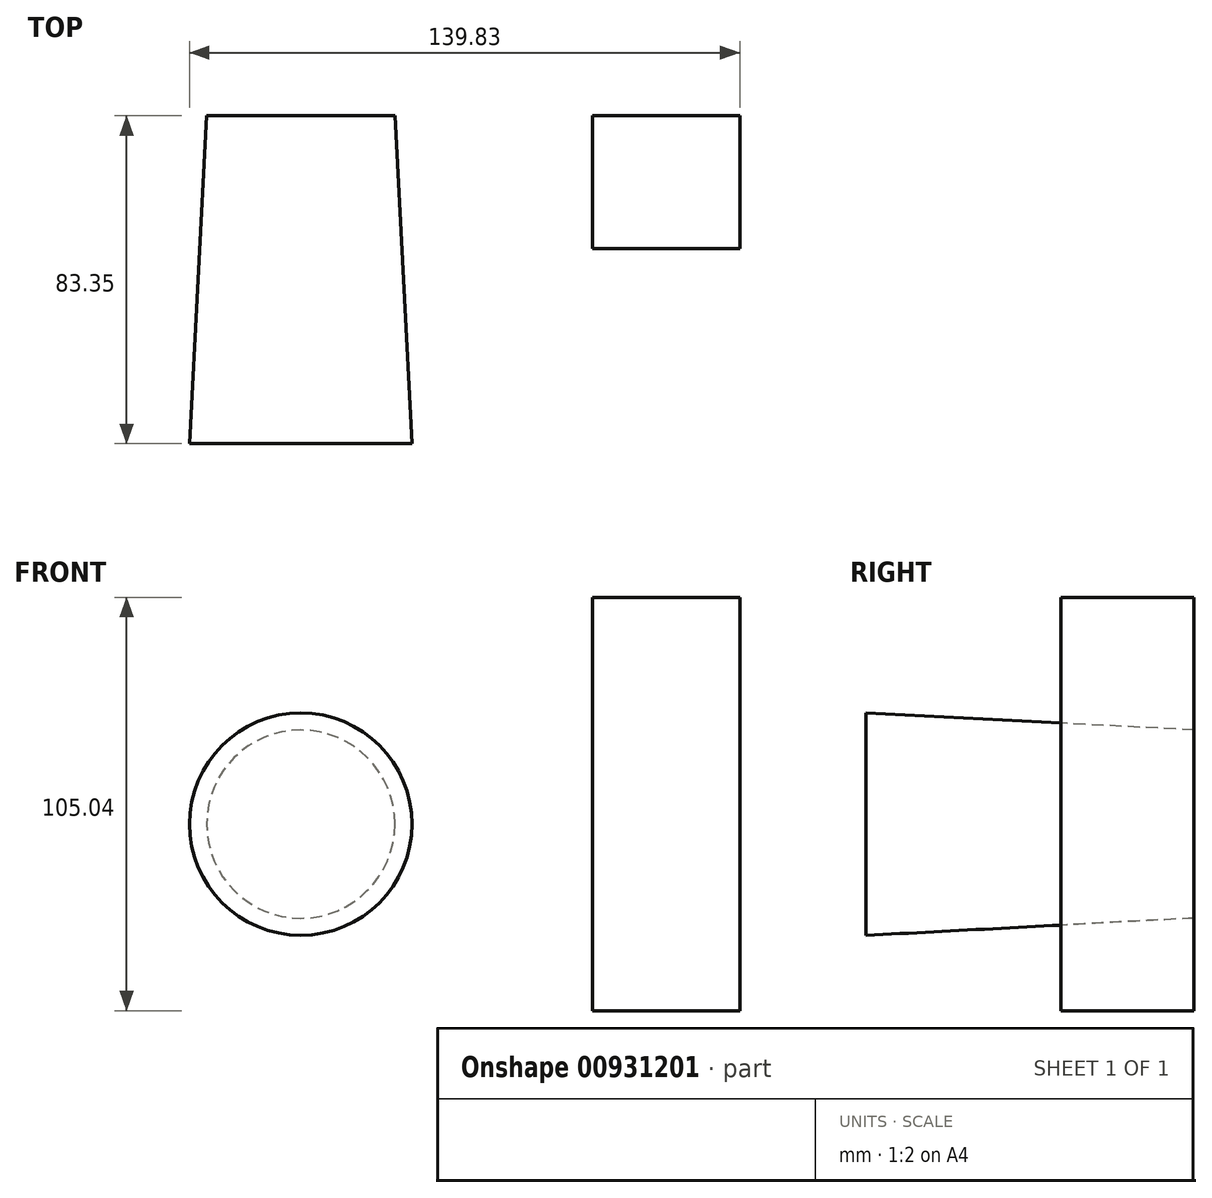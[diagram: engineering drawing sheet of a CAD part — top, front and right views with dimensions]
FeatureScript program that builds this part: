
annotation { "Feature Type Name" : "Feature", "Feature Type Description" : "" }
export const myFeature = defineFeature(function(context is Context, id is Id, definition is map)
    precondition{}
    {
        {
            var Q0;
            Q0=qCreatedBy(makeId("Front.planeOp"),FACE);
            var sketch = newSketch(context, id + "F0", { "sketchPlane" : qUnion([Q0])});
            skCircle(sketch, "E0", {"center": v(-41.24, 47.4) * mm, "radius": 23.9 * mm});
            skSolve(sketch);
        }
        {
            var Q0;
            Q0 = qSketchRegion(id + "F0", true);
            extrude(context, id + "F1", {"entities" : qUnion([Q0]), "depth" : 83.35 * mm, "offsetDistance" : 25.4 * mm, "hasDraft" : true, "draftAngle" : 3 * degree});
        }
        {
            var Q0;
            Q0=qCreatedBy(makeId("Front.planeOp"),FACE);
            var sketch = newSketch(context, id + "F2", { "sketchPlane" : qUnion([Q0])});
            skLineSegment(sketch, "E1.bottom", {"start": v(32.82, 105.04) * mm, "end": v(70.32, 105.04) * mm});
            skLineSegment(sketch, "E1.top", {"start": v(32.82, 0) * mm, "end": v(70.32, 0) * mm});
            skLineSegment(sketch, "E1.left", {"start": v(32.82, 105.04) * mm, "end": v(32.82, 0) * mm});
            skLineSegment(sketch, "E1.right", {"start": v(70.32, 105.04) * mm, "end": v(70.32, 0) * mm});
            skSolve(sketch);
        }
        {
            var Q0;
            Q0=makeQuery(id+"F2.imprint","IMPRINT",FACE,{"disambiguationData":[TD([[makeQuery(id+"F2.imprint","IMPRINT",EDGE,{"derivedFrom":sQuery(id+"F2.wireOp",EDGE,"E1.bottom")}),-1.0]])]});
            var sketch = newSketch(context, id + "F3", { "sketchPlane" : qUnion([Q0])});
            skSolve(sketch);
        }
        {
            var Q0;
            Q0=makeQuery(id+"F3.imprint","IMPRINT",FACE,{"disambiguationData":[TD([[makeQuery(id+"F3.imprint","IMPRINT",EDGE,{"derivedFrom":makeQuery(id+"F2.imprint","IMPRINT",EDGE,{"derivedFrom":sQuery(id+"F2.wireOp",EDGE,"E1.bottom")})}),-1.0]])]});
            extrude(context, id + "F4", {"entities" : qUnion([Q0]), "depth" : 33.8 * mm, "offsetDistance" : 25.4 * mm});
        }
    });
